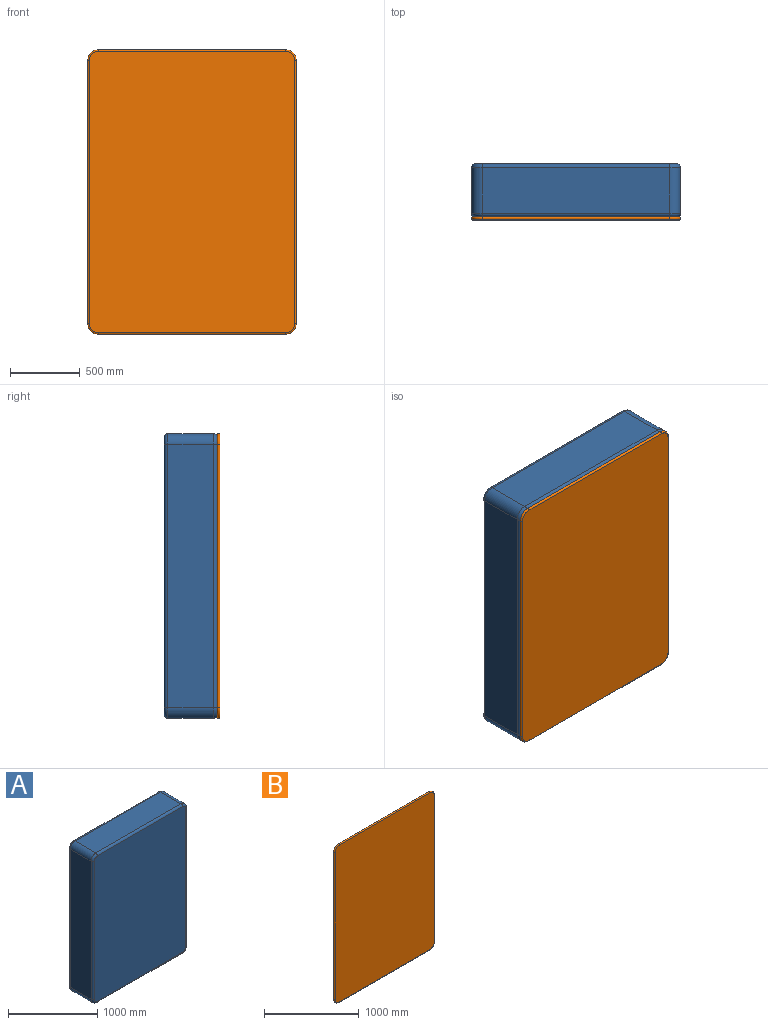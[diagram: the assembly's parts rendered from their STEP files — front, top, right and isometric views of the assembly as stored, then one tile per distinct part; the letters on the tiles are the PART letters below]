
ASSEMBLY  parts=2 mates=1
PART A: 26 faces, bbox 1511.2x381x2057.3 mm
  f0: plane 1892.3x330.2mm, normal (-1,0,0), area 624837.5mm2, adj f1,f7,f14,f22
  f1: cylinder r=76.2mm len=330.2mm, axis (0,1,0), area 39523.2mm2, adj f0,f2,f12,f20
  f2: plane 1346.2x330.2mm, normal (0,0,-1), area 444515.2mm2, adj f1,f3,f10,f18
  f3: cylinder r=76.2mm len=330.2mm, axis (0,1,0), area 39523.2mm2, adj f2,f4,f11,f19
  f4: plane 1892.3x330.2mm, normal (1,0,0), area 624837.5mm2, adj f3,f5,f13,f21
  f5: cylinder r=76.2mm len=330.2mm, axis (0,1,0), area 39523.2mm2, adj f4,f6,f15,f23
  f6: plane 1346.2x330.2mm, normal (0,0,1), area 444515.2mm2, adj f5,f7,f17,f25
  f7: cylinder r=76.2mm len=330.2mm, axis (0,1,0), area 39523.2mm2, adj f0,f6,f16,f24
  f8: plane 1993.9x1447.8mm, normal (0,-1,0), area 2884553.2mm2, adj f18,f19,f20,f21,f22,f23,f24,f25
  f9: plane 1993.9x1447.8mm, normal (0,1,0), area 2884553.2mm2, adj f10,f11,f12,f13,f14,f15,f16,f17
  f10: cylinder r=25.4mm len=1346.2mm, axis (1,0,0), area 53711mm2, adj f2,f9,f11,f12
  f11: torus R=50.8mm, axis (0,-1,0), area 4197.2mm2, adj f3,f9,f10,f13
  f12: torus R=50.8mm, axis (0,-1,0), area 4197.2mm2, adj f1,f9,f10,f14
  f13: cylinder r=25.4mm len=1892.3mm, axis (0,0,1), area 75499.4mm2, adj f4,f9,f11,f15
  f14: cylinder r=25.4mm len=1892.3mm, axis (0,0,-1), area 75499.4mm2, adj f0,f9,f12,f16
  f15: torus R=50.8mm, axis (0,-1,0), area 4197.2mm2, adj f5,f9,f13,f17
  f16: torus R=50.8mm, axis (0,-1,0), area 4197.2mm2, adj f7,f9,f14,f17
  f17: cylinder r=25.4mm len=1346.2mm, axis (-1,0,0), area 53711mm2, adj f6,f9,f15,f16
  f18: cylinder r=25.4mm len=1346.2mm, axis (-1,0,0), area 53711mm2, adj f2,f8,f19,f20
  f19: torus R=50.8mm, axis (0,-1,0), area 4197.2mm2, adj f3,f8,f18,f21
  f20: torus R=50.8mm, axis (0,-1,0), area 4197.2mm2, adj f1,f8,f18,f22
  f21: cylinder r=25.4mm len=1892.3mm, axis (0,0,-1), area 75499.4mm2, adj f4,f8,f19,f23
  f22: cylinder r=25.4mm len=1892.3mm, axis (0,0,1), area 75499.4mm2, adj f0,f8,f20,f24
  f23: torus R=50.8mm, axis (0,-1,0), area 4197.2mm2, adj f5,f8,f21,f25
  f24: torus R=50.8mm, axis (0,-1,0), area 4197.2mm2, adj f7,f8,f22,f25
  f25: cylinder r=25.4mm len=1346.2mm, axis (1,0,0), area 53711mm2, adj f6,f8,f23,f24
PART B: 10 faces, bbox 1511.2x19.1x2057.3 mm
  f0: plane 2025.65x1479.55mm, normal (0,-1,0), area 2993234.4mm2, adj f2,f3,f4,f5,f6,f7,f8,f9
  f1: plane 2025.65x1479.55mm, normal (0,1,0), area 2993234.4mm2, adj f2,f3,f4,f5,f6,f7,f8,f9
  f2: cylinder r=9.53mm len=1346.2mm, axis (-1,0,0), area 40283.2mm2, adj f0,f1,f3,f4
  f3: torus R=66.67mm, axis (0,-1,0), area 3419mm2, adj f0,f1,f2,f5
  f4: torus R=66.67mm, axis (0,-1,0), area 3419mm2, adj f0,f1,f2,f6
  f5: cylinder r=9.53mm len=1892.3mm, axis (0,0,-1), area 56624.6mm2, adj f0,f1,f3,f7
  f6: cylinder r=9.53mm len=1892.3mm, axis (0,0,1), area 56624.6mm2, adj f0,f1,f4,f8
  f7: torus R=66.67mm, axis (0,-1,0), area 3419mm2, adj f0,f1,f5,f9
  f8: torus R=66.67mm, axis (0,-1,0), area 3419mm2, adj f0,f1,f6,f9
  f9: cylinder r=9.53mm len=1346.2mm, axis (1,0,0), area 40283.2mm2, adj f0,f1,f7,f8
PLACE A t=(-2250.57,1035.53,-93.89)mm
PLACE B rot(axis=(1,0,0),180deg) t=(1444.69,635.48,2754.25)mm
MATE fastened B.f0 <-> A.f8  axis (0,1,0) through (-2962.94,654.53,652.78)mm
